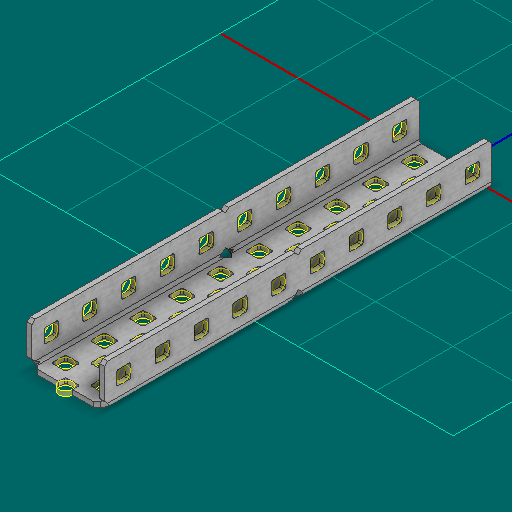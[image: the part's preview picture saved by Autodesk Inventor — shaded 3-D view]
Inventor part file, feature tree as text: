
AUTODESK INVENTOR PART (.ipt)
format: ipt  version: 2025 (Build 290162000, 162)  size: 1,000,448 bytes
history: native  units: in
note: dims shown in document units (in); Inventor stores cm internally (conversion verified against a paired STEP export)
features: other x106, sketch x5, sheet_metal_op x1
ambient origin geometry x8: Origin, YZ Plane, XZ Plane, XY Plane, X Axis, Y Axis, Z Axis, Center Point
bodies: Solid1 (feature_tree)
feature tree (112):
  other  "Alu C 1x2x1x10.ipt"
  other  "Solid1::Alu C 1x2x1x10.ipt"
  other  "TaggingFeature1"
  sketch  "Sketch1"  dims[d0=0.3937in]
  sketch  "Sketch2"  dims[d1=0.0625in]
  sketch  "Sketch3"
  other  "Flange Pattern Sketch"
  sketch  "Sketch9"
  sheet_metal_op  "Body Pattern Sketch"
  other  "Arc Length"
  sketch  "Sketch14"
  other  "Flange Pattern Plane"
  other  "Srf1"
  other  "Srf2"
  other  "Srf3"
  other  "Srf4"
  other  "Srf5"
  other  "Srf6"
  other  "Srf7"
  other  "Srf8"
  other  "Srf9"
  other  "Srf10"
  other  "Srf11"
  other  "Srf12"
  other  "Srf13"
  other  "Srf14"
  other  "Srf15"
  other  "Srf16"
  other  "Srf17"
  other  "Srf18"
  other  "Srf19"
  other  "Srf20"
  other  "Srf21"
  other  "Srf22"
  other  "Srf23"
  other  "Srf24"
  other  "Srf25"
  other  "Srf26"
  other  "Srf27"
  other  "Srf28"
  other  "Srf29"
  other  "Srf30"
  other  "Srf31"
  other  "Srf32"
  other  "Srf33"
  other  "Srf34"
  other  "Srf35"
  other  "Srf36"
  other  "Srf37"
  other  "Srf38"
  other  "Srf39"
  other  "Srf40"
  other  "Srf41"
  other  "Srf42"
  other  "Srf43"
  other  "Srf44"
  other  "Srf45"
  other  "Srf46"
  other  "Srf47"
  other  "Srf48"
  other  "Srf49"
  other  "Srf50"
  other  "Srf1::Derived"
  other  "Srf2::Derived"
  other  "Srf823::Derived"
  other  "Srf824::Derived"
  other  "Srf825::Derived"
  other  "Srf826::Derived"
  other  "Srf827::Derived"
  other  "Srf828::Derived"
  other  "Srf829::Derived"
  other  "Srf922::Derived"
  other  "Srf923::Derived"
  other  "Srf924::Derived"
  other  "Srf925::Derived"
  other  "Srf926::Derived"
  other  "Srf1143::Derived"
  other  "Srf1144::Derived"
  other  "Srf1145::Derived"
  other  "Srf1146::Derived"
  other  "Srf1147::Derived"
  other  "Srf1148::Derived"
  other  "Srf91::Derived"
  other  "Srf92::Derived"
  other  "Srf856::Derived"
  other  "Srf857::Derived"
  other  "Srf858::Derived"
  other  "Srf859::Derived"
  other  "Srf860::Derived"
  other  "Srf861::Derived"
  other  "Srf862::Derived"
  other  "Srf959::Derived"
  other  "Srf960::Derived"
  other  "Srf961::Derived"
  other  "Srf962::Derived"
  other  "Srf963::Derived"
  other  "Srf1199::Derived"
  other  "Srf1200::Derived"
  other  "Srf1201::Derived"
  other  "Srf1202::Derived"
  other  "Srf1203::Derived"
  other  "Srf1204::Derived"
  other  "Srf786::Derived"
  other  "Srf889::Derived"
  other  "Srf890::Derived"
  other  "Srf891::Derived"
  other  "Srf892::Derived"
  other  "Srf893::Derived"
  other  "Srf894::Derived"
  other  "Srf895::Derived"
  other  "Srf896::Derived"
  other  "Srf996::Derived"
